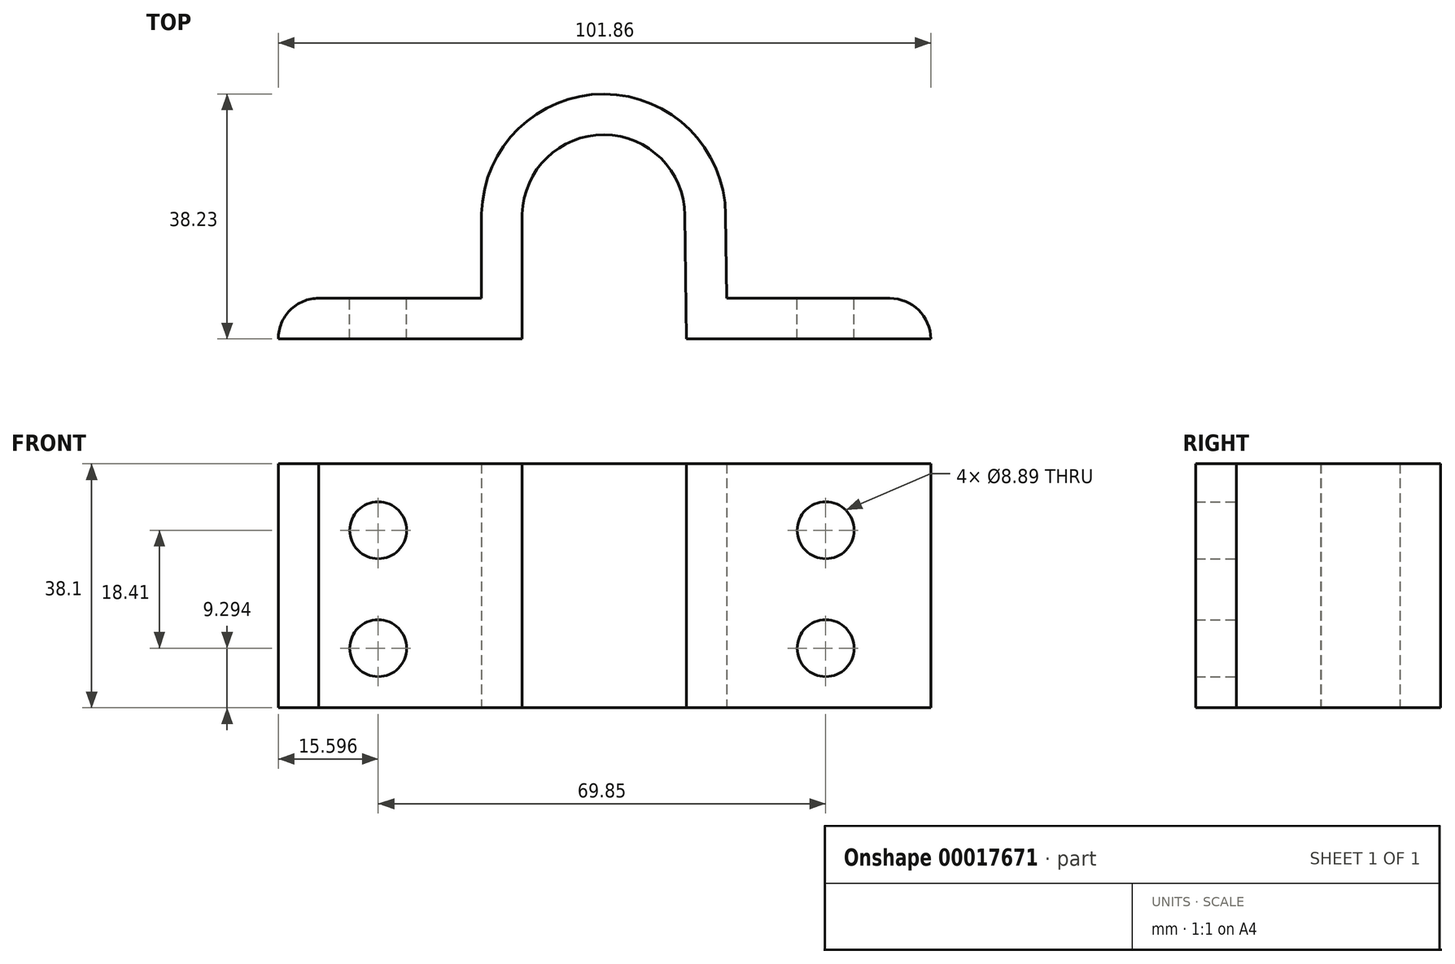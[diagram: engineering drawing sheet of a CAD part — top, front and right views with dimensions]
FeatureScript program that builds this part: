
annotation { "Feature Type Name" : "Feature", "Feature Type Description" : "" }
export const myFeature = defineFeature(function(context is Context, id is Id, definition is map)
    precondition{}
    {
        {
            var Q0;
            Q0=qCreatedBy(makeId("Top.planeOp"),FACE);
            var sketch = newSketch(context, id + "F0", { "sketchPlane" : qUnion([Q0])});
            skLineSegment(sketch, "E0", {"start": v(-44.5, 0) * mm, "end": v(44.58, 0) * mm, "construction": true});
            skLineSegment(sketch, "E1", {"start": v(-44.5, 31.88) * mm, "end": v(54.46, 31.88) * mm, "construction": true});
            skLineSegment(sketch, "E2", {"start": v(0, 0) * mm, "end": v(0, 31.88) * mm, "construction": true});
            skArc(sketch, "E3", {"start": v(12.64, 19.3) * mm, "mid": v(8.9, 28.18) * mm, "end": v(0, 31.88) * mm});
            skArc(sketch, "E4", {"start": v(0, 31.88) * mm, "mid": v(-8.92, 28.28) * mm, "end": v(-12.76, 19.47) * mm});
            skLineSegment(sketch, "E5", {"start": v(-12.76, 19.47) * mm, "end": v(-12.76, 0) * mm});
            skLineSegment(sketch, "E6", {"start": v(12.64, 19.3) * mm, "end": v(12.83, 0) * mm});
            skLineSegment(sketch, "E7", {"start": v(12.83, 0) * mm, "end": v(44.58, 0) * mm});
            skLineSegment(sketch, "E8", {"start": v(-12.76, 0) * mm, "end": v(-44.5, 0) * mm});
            skLineSegment(sketch, "E9.0", {"start": v(19.12, 6.35) * mm, "end": v(44.58, 6.35) * mm});
            skLineSegment(sketch, "E9.1", {"start": v(18.99, 19.37) * mm, "end": v(19.12, 6.35) * mm});
            skArc(sketch, "E9.2", {"start": v(18.99, 19.37) * mm, "mid": v(13.37, 32.68) * mm, "end": v(0.03, 38.23) * mm});
            skArc(sketch, "E9.3", {"start": v(0.03, 38.23) * mm, "mid": v(-13.37, 32.8) * mm, "end": v(-19.1, 19.53) * mm});
            skLineSegment(sketch, "E9.4", {"start": v(-19.1, 19.53) * mm, "end": v(-19.1, 6.35) * mm});
            skLineSegment(sketch, "E9.5", {"start": v(-19.1, 6.35) * mm, "end": v(-44.5, 6.35) * mm});
            skLineSegment(sketch, "E10", {"start": v(-44.5, 0) * mm, "end": v(-44.5, 0.02) * mm});
            skArc(sketch, "E11", {"start": v(-44.5, 6.35) * mm, "mid": v(-49, 4.49) * mm, "end": v(-50.84, 0) * mm});
            skArc(sketch, "E12", {"start": v(44.58, 6.35) * mm, "mid": v(49.1, 4.5) * mm, "end": v(51.02, 0) * mm});
            skLineSegment(sketch, "E13", {"start": v(44.58, 0) * mm, "end": v(51.02, 0) * mm});
            skLineSegment(sketch, "E14", {"start": v(-44.5, 0.02) * mm, "end": v(-50.84, 0) * mm});
            skSolve(sketch);
        }
        {
            var Q0;
            Q0=makeQuery(id+"F0.imprint","IMPRINT",FACE,{"disambiguationData":[TD([[makeQuery(id+"F0.imprint","IMPRINT",EDGE,{"derivedFrom":sQuery(id+"F0.wireOp",EDGE,"E3")}),-1.0]])]});
            extrude(context, id + "F1", {"entities" : qUnion([Q0]), "depth" : 38.1 * mm});
        }
        {
            var Q0;
            Q0=makeQuery(id+"F1.opExtrude","SWEPT_FACE",FACE,{"disambiguationData":[OSD([sQuery(id+"F0.wireOp",EDGE,"E9.0")])]});
            var sketch = newSketch(context, id + "F2", { "sketchPlane" : qUnion([Q0])});
            skCircle(sketch, "E15", {"center": v(-34.6, 27.7) * mm, "radius": 4.45 * mm});
            skCircle(sketch, "E16.0.1.0", {"center": v(-34.6, 9.3) * mm, "radius": 4.45 * mm});
            skCircle(sketch, "E16.1.0.0", {"center": v(35.24, 27.7) * mm, "radius": 4.45 * mm});
            skCircle(sketch, "E16.1.1.0", {"center": v(35.24, 9.3) * mm, "radius": 4.45 * mm});
            skLineSegment(sketch, "E16.direction1", {"start": v(-34.6, 27.7) * mm, "end": v(35.24, 27.7) * mm, "construction": true});
            skLineSegment(sketch, "E16.direction2", {"start": v(-34.6, 27.7) * mm, "end": v(-34.6, 9.3) * mm, "construction": true});
            skSolve(sketch);
        }
        {
            var Q0;
            Q0 = qSketchRegion(id + "F2", true);
            extrude(context, id + "F3", {"entities" : qUnion([Q0]), "operationType" : NewBodyOperationType.REMOVE, "endBound" : BoundingType.THROUGH_ALL, "oppositeDirection" : true, "depth" : 25.4 * mm});
        }
    });
